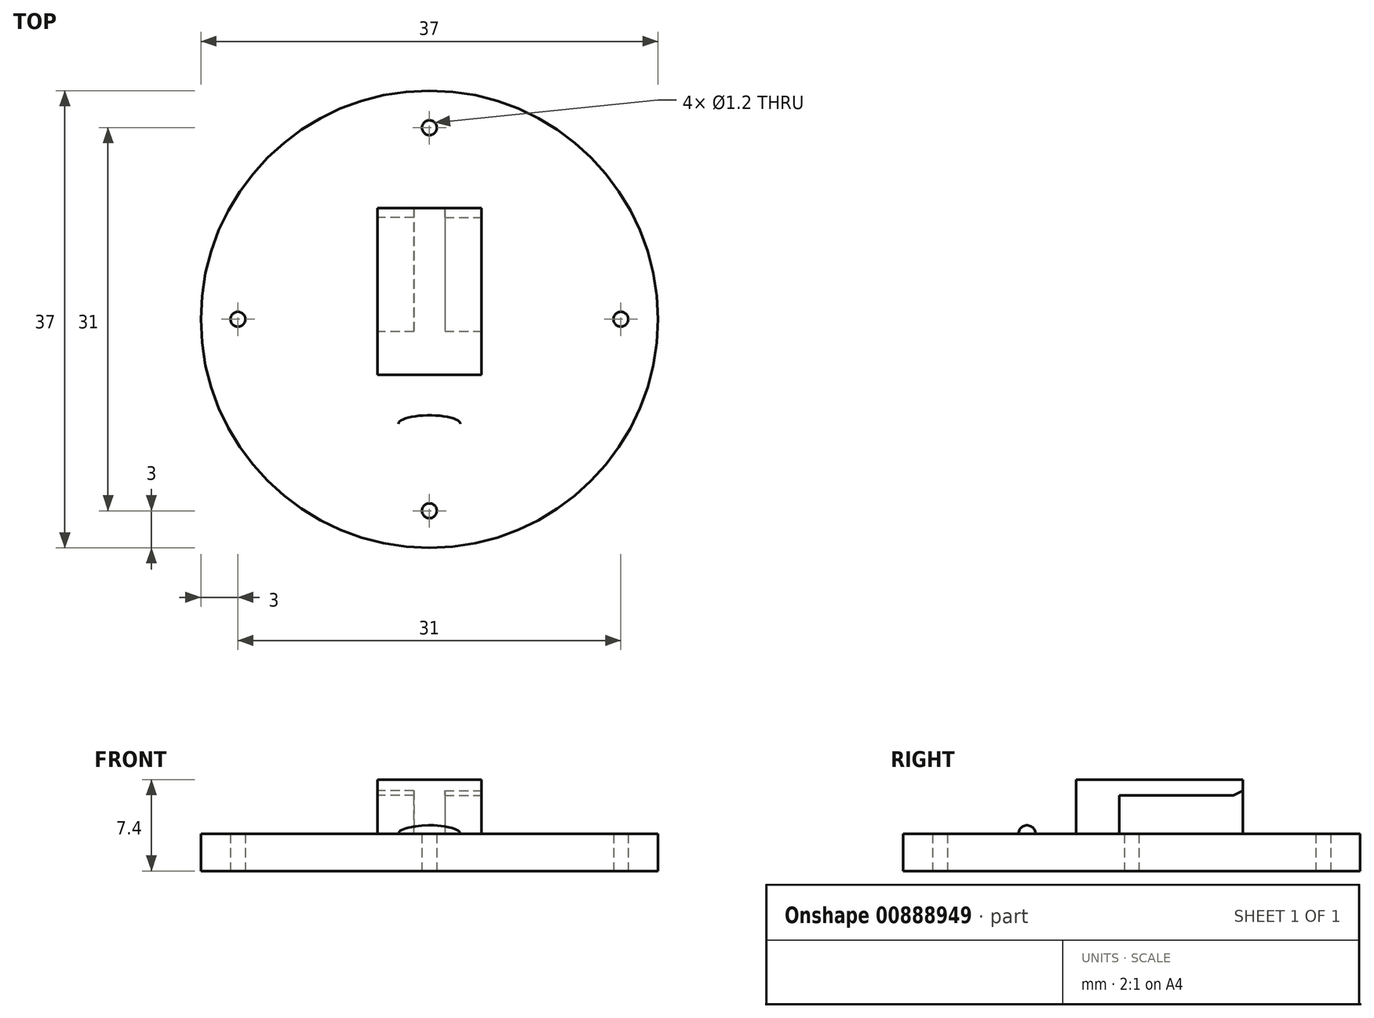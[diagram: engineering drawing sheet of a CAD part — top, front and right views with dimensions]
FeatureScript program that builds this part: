
annotation { "Feature Type Name" : "Feature", "Feature Type Description" : "" }
export const myFeature = defineFeature(function(context is Context, id is Id, definition is map)
    precondition{}
    {
        {
            var Q0;
            Q0=qCreatedBy(makeId("Top.planeOp"),FACE);
            var sketch = newSketch(context, id + "F0", { "sketchPlane" : qUnion([Q0])});
            skCircle(sketch, "E0", {"center": v(0, 0) * mm, "radius": 18.5 * mm});
            skCircle(sketch, "E1", {"center": v(0, 15.5) * mm, "radius": 0.6 * mm});
            skCircle(sketch, "E2.1.0", {"center": v(15.5, 0) * mm, "radius": 0.6 * mm});
            skCircle(sketch, "E2.2.0", {"center": v(0, -15.5) * mm, "radius": 0.6 * mm});
            skCircle(sketch, "E2.3.0", {"center": v(-15.5, 0) * mm, "radius": 0.6 * mm});
            skLineSegment(sketch, "E2.anchor1", {"start": v(0, 0) * mm, "end": v(0, 15.5) * mm, "construction": true});
            skLineSegment(sketch, "E2.anchor2", {"start": v(0, 0) * mm, "end": v(-15.5, 0) * mm, "construction": true});
            skSolve(sketch);
        }
        {
            var Q0;
            Q0=makeQuery(id+"F0.imprint","IMPRINT",FACE,{"disambiguationData":[TD([[makeQuery(id+"F0.imprint","IMPRINT",EDGE,{"derivedFrom":sQuery(id+"F0.wireOp",EDGE,"E0")}),1.0]])]});
            extrude(context, id + "F1", {"entities" : qUnion([Q0]), "depth" : 3 * mm, "offsetDistance" : 25 * mm});
        }
        {
            var Q0;
            Q0=makeQuery(id+"F1.opExtrude","CAP_FACE",FACE,{"disambiguationData":[OSD([sQuery(id+"F0.wireOp",EDGE,"E0"),sQuery(id+"F0.wireOp",EDGE,"E1"),sQuery(id+"F0.wireOp",EDGE,"E2.1.0"),sQuery(id+"F0.wireOp",EDGE,"E2.2.0"),sQuery(id+"F0.wireOp",EDGE,"E2.3.0")])],"isStart":false});
            var sketch = newSketch(context, id + "F2", { "sketchPlane" : qUnion([Q0])});
            skLineSegment(sketch, "E3.bottom", {"start": v(-4.2, 9) * mm, "end": v(4.2, 9) * mm});
            skLineSegment(sketch, "E3.top", {"start": v(-4.2, -4.5) * mm, "end": v(4.2, -4.5) * mm});
            skLineSegment(sketch, "E3.left", {"start": v(-4.2, 9) * mm, "end": v(-4.2, -4.5) * mm});
            skLineSegment(sketch, "E3.right", {"start": v(4.2, 9) * mm, "end": v(4.2, -4.5) * mm});
            skSolve(sketch);
        }
        {
            var Q0;
            Q0=makeQuery(id+"F2.imprint","IMPRINT",FACE,{"disambiguationData":[TD([[makeQuery(id+"F2.imprint","IMPRINT",EDGE,{"derivedFrom":sQuery(id+"F2.wireOp",EDGE,"E3.bottom")}),-1.0]])]});
            extrude(context, id + "F3", {"entities" : qUnion([Q0]), "operationType" : NewBodyOperationType.ADD, "depth" : 4.4 * mm, "offsetDistance" : 25 * mm});
        }
        {
            var Q0;
            Q0=makeQuery(id+"F3.opExtrude","SWEPT_FACE",FACE,{"disambiguationData":[OSD([sQuery(id+"F2.wireOp",EDGE,"E3.left")])]});
            var sketch = newSketch(context, id + "F4", { "sketchPlane" : qUnion([Q0])});
            skLineSegment(sketch, "E4", {"start": v(1, 3) * mm, "end": v(1, 6.1) * mm});
            skLineSegment(sketch, "E5", {"start": v(-9, 3) * mm, "end": v(1, 3) * mm});
            skLineSegment(sketch, "E6", {"start": v(1, 6.1) * mm, "end": v(-8.23, 6.1) * mm});
            skLineSegment(sketch, "E7", {"start": v(-8.23, 6.1) * mm, "end": v(-9, 6.5) * mm});
            skLineSegment(sketch, "E8", {"start": v(-9, 6.5) * mm, "end": v(-9, 3) * mm});
            skSolve(sketch);
        }
        {
            var Q0;
            Q0=makeQuery(id+"F4.imprint","IMPRINT",FACE,{"disambiguationData":[TD([[makeQuery(id+"F4.imprint","IMPRINT",EDGE,{"derivedFrom":sQuery(id+"F4.wireOp",EDGE,"E4")}),1.0]])]});
            extrude(context, id + "F5", {"entities" : qUnion([Q0]), "operationType" : NewBodyOperationType.REMOVE, "oppositeDirection" : true, "depth" : 2.95 * mm, "offsetDistance" : 25 * mm});
        }
        {
            var Q0;
            Q0=makeQuery(id+"F3.opExtrude","SWEPT_FACE",FACE,{"disambiguationData":[OSD([sQuery(id+"F2.wireOp",EDGE,"E3.right")])]});
            var sketch = newSketch(context, id + "F6", { "sketchPlane" : qUnion([Q0])});
            skLineSegment(sketch, "E9", {"start": v(9, 3) * mm, "end": v(9, 6.5) * mm});
            skLineSegment(sketch, "E10", {"start": v(-1, 3) * mm, "end": v(9, 3) * mm});
            skLineSegment(sketch, "E11", {"start": v(-1, 6.1) * mm, "end": v(-1, 3) * mm});
            skLineSegment(sketch, "E12", {"start": v(-0.22, 6.1) * mm, "end": v(-1, 6.1) * mm});
            skLineSegment(sketch, "E13", {"start": v(-0.22, 6.1) * mm, "end": v(8.23, 6.1) * mm});
            skLineSegment(sketch, "E14", {"start": v(8.23, 6.1) * mm, "end": v(9, 6.5) * mm});
            skSolve(sketch);
        }
        {
            var Q0;
            {var subQ1=sQuery(id+"F6.wireOp",EDGE,"E11");Q0=makeQuery(id+"F6.imprint","IMPRINT",FACE,{"disambiguationData":[TD([[makeQuery(id+"F6.imprint","IMPRINT",EDGE,{"derivedFrom":subQ1}),1.0]])]});}
            extrude(context, id + "F7", {"entities" : qUnion([Q0]), "operationType" : NewBodyOperationType.REMOVE, "oppositeDirection" : true, "depth" : 2.95 * mm, "offsetDistance" : 25 * mm});
        }
        {
            var Q0;
            Q0=makeQuery(id+"F7.boolean.opBoolean","MERGE",FACE,{"derivedFrom":[makeQuery(id+"F5.boolean.opBoolean","MERGE",FACE,{"derivedFrom":[makeQuery(id+"F1.opExtrude","CAP_FACE",FACE,{"disambiguationData":[OSD([sQuery(id+"F0.wireOp",EDGE,"E0"),sQuery(id+"F0.wireOp",EDGE,"E1"),sQuery(id+"F0.wireOp",EDGE,"E2.1.0"),sQuery(id+"F0.wireOp",EDGE,"E2.2.0"),sQuery(id+"F0.wireOp",EDGE,"E2.3.0")])],"isStart":false})],"fromTools":[makeQuery(id+"F5.opExtrude","SWEPT_FACE",FACE,{"disambiguationData":[OSD([sQuery(id+"F4.wireOp",EDGE,"E5")])]})]})],"fromTools":[makeQuery(id+"F7.opExtrude","SWEPT_FACE",FACE,{"disambiguationData":[OSD([sQuery(id+"F6.wireOp",EDGE,"E10")])]})]});
            var sketch = newSketch(context, id + "F8", { "sketchPlane" : qUnion([Q0])});
            skEllipse(sketch, "E15", {"center": v(0, -8.47) * mm, "majorRadius": 2.5 * mm, "minorRadius": 0.7 * mm, "majorAxis": v(-1, 0)});
            skLineSegment(sketch, "E16", {"start": v(-2.5, -8.47) * mm, "end": v(2.5, -8.47) * mm});
            skSolve(sketch);
        }
        {
            var Q0;
            {var subQ0=sQuery(id+"F8.wireOp",EDGE,"E16");Q0=makeQuery(id+"F8.imprint","IMPRINT",FACE,{"disambiguationData":[TD([[makeQuery(id+"F8.imprint","IMPRINT",EDGE,{"derivedFrom":subQ0}),-1.0]])]});}
            var Q1;
            Q1=sQuery(id+"F8.wireOp",EDGE,"E16");
            revolve(context, id + "F9", {"operationType" : NewBodyOperationType.ADD, "surfaceOperationType" : NewSurfaceOperationType.NEW, "entities" : qUnion([Q0]), "axis" : qUnion([Q1]), "revolveType" : RevolveType.FULL});
        }
    });
